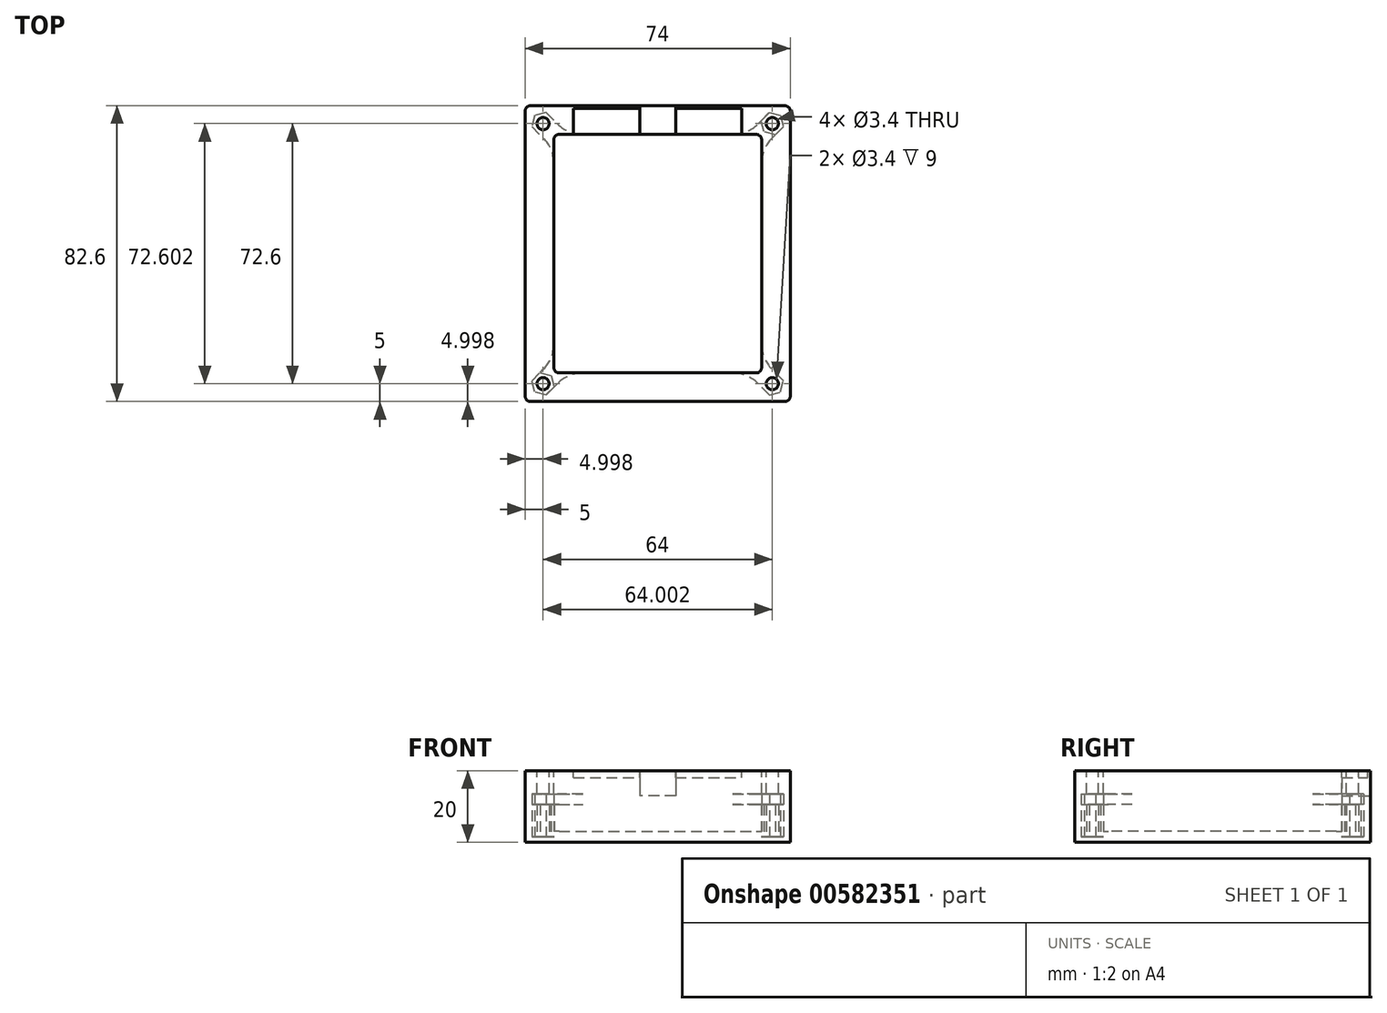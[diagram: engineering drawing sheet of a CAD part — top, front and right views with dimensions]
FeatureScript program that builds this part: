
annotation { "Feature Type Name" : "Feature", "Feature Type Description" : "" }
export const myFeature = defineFeature(function(context is Context, id is Id, definition is map)
    precondition{}
    {
        {
            var Q0;
            Q0=qCreatedBy(makeId("Top.planeOp"),FACE);
            var sketch = newSketch(context, id + "F0", { "sketchPlane" : qUnion([Q0])});
            skLineSegment(sketch, "E0.top", {"start": v(-37, -41.3) * mm, "end": v(37, -41.3) * mm});
            skLineSegment(sketch, "E0.left", {"start": v(-37, 31.3) * mm, "end": v(-37, -41.3) * mm});
            skLineSegment(sketch, "E0.right", {"start": v(37, 31.3) * mm, "end": v(37, -41.3) * mm});
            skLineSegment(sketch, "E1.top", {"start": v(-37, 41.3) * mm, "end": v(37, 41.3) * mm});
            skLineSegment(sketch, "E1.left", {"start": v(-37, 31.3) * mm, "end": v(-37, 41.3) * mm});
            skLineSegment(sketch, "E1.right", {"start": v(37, 31.3) * mm, "end": v(37, 41.3) * mm});
            skCircle(sketch, "E2", {"center": v(-32, 36.3) * mm, "radius": 1.7 * mm});
            skCircle(sketch, "E3.MirrorC", {"center": v(32, 36.3) * mm, "radius": 1.7 * mm});
            skCircle(sketch, "E4.MirrorC", {"center": v(32, -36.3) * mm, "radius": 1.7 * mm});
            skCircle(sketch, "E5.MirrorC", {"center": v(-32, -36.3) * mm, "radius": 1.7 * mm});
            skLineSegment(sketch, "E6", {"start": v(-37, 0) * mm, "end": v(37, 0) * mm, "construction": true});
            skLineSegment(sketch, "E7", {"start": v(0, 41.3) * mm, "end": v(0, -41.3) * mm, "construction": true});
            skLineSegment(sketch, "E8.0", {"start": v(-29, 33.3) * mm, "end": v(29, 33.3) * mm});
            skLineSegment(sketch, "E8.1", {"start": v(-29, 33.3) * mm, "end": v(-29, -33.3) * mm});
            skLineSegment(sketch, "E8.2", {"start": v(-29, -33.3) * mm, "end": v(29, -33.3) * mm});
            skLineSegment(sketch, "E8.3", {"start": v(29, 33.3) * mm, "end": v(29, -33.3) * mm});
            skCircle(sketch, "E9.cCircle", {"center": v(-32, -36.3) * mm, "radius": 2.8 * mm, "construction": true});
            skLineSegment(sketch, "E9.0", {"start": v(-35.13, -35.47) * mm, "end": v(-32.84, -33.18) * mm});
            skLineSegment(sketch, "E9.1", {"start": v(-32.84, -33.18) * mm, "end": v(-29.72, -34.02) * mm});
            skLineSegment(sketch, "E9.2", {"start": v(-29.72, -34.02) * mm, "end": v(-28.88, -37.14) * mm});
            skLineSegment(sketch, "E9.3", {"start": v(-28.88, -37.14) * mm, "end": v(-31.17, -39.43) * mm});
            skLineSegment(sketch, "E9.4", {"start": v(-31.17, -39.43) * mm, "end": v(-34.29, -38.59) * mm});
            skLineSegment(sketch, "E9.5", {"start": v(-34.29, -38.59) * mm, "end": v(-35.13, -35.47) * mm});
            skPoint(sketch, "E9.0.midPoint", {"position": v(-33.98, -34.32) * mm});
            skLineSegment(sketch, "E10", {"start": v(-37, -41.3) * mm, "end": v(-29, -33.3) * mm, "construction": true});
            skLineSegment(sketch, "E11", {"start": v(-32.84, -33.18) * mm, "end": v(-29, -29.34) * mm});
            skLineSegment(sketch, "E12", {"start": v(-28.88, -37.14) * mm, "end": v(-25.04, -33.3) * mm});
            skLineSegment(sketch, "E13.MirrorCS", {"start": v(29.72, -34.02) * mm, "end": v(28.88, -37.14) * mm});
            skLineSegment(sketch, "E14.MirrorCS", {"start": v(32.84, -33.18) * mm, "end": v(29.72, -34.02) * mm});
            skLineSegment(sketch, "E15.MirrorCS", {"start": v(28.88, -37.14) * mm, "end": v(25.04, -33.3) * mm});
            skLineSegment(sketch, "E16.MirrorCS", {"start": v(28.88, -37.14) * mm, "end": v(31.17, -39.43) * mm});
            skLineSegment(sketch, "E17.MirrorCS", {"start": v(31.17, -39.43) * mm, "end": v(34.29, -38.59) * mm});
            skLineSegment(sketch, "E18.MirrorCS", {"start": v(34.29, -38.59) * mm, "end": v(35.13, -35.47) * mm});
            skLineSegment(sketch, "E19.MirrorCS", {"start": v(32.84, -33.18) * mm, "end": v(29, -29.34) * mm});
            skLineSegment(sketch, "E20.MirrorCS", {"start": v(35.13, -35.47) * mm, "end": v(32.84, -33.18) * mm});
            skLineSegment(sketch, "E21.MirrorCS", {"start": v(35.13, 35.47) * mm, "end": v(32.84, 33.18) * mm});
            skLineSegment(sketch, "E22.MirrorCS", {"start": v(34.29, 38.59) * mm, "end": v(35.13, 35.47) * mm});
            skLineSegment(sketch, "E23.MirrorCS", {"start": v(31.17, 39.43) * mm, "end": v(34.29, 38.59) * mm});
            skLineSegment(sketch, "E24.MirrorCS", {"start": v(28.88, 37.14) * mm, "end": v(31.17, 39.43) * mm});
            skLineSegment(sketch, "E25.MirrorCS", {"start": v(28.88, 37.14) * mm, "end": v(25.04, 33.3) * mm});
            skLineSegment(sketch, "E26.MirrorCS", {"start": v(29.72, 34.02) * mm, "end": v(28.88, 37.14) * mm});
            skLineSegment(sketch, "E27.MirrorCS", {"start": v(32.84, 33.18) * mm, "end": v(29.72, 34.02) * mm});
            skLineSegment(sketch, "E28.MirrorCS", {"start": v(32.84, 33.18) * mm, "end": v(29, 29.34) * mm});
            skLineSegment(sketch, "E29.MirrorCS", {"start": v(-35.13, 35.47) * mm, "end": v(-32.84, 33.18) * mm});
            skPoint(sketch, "E30.MirrorP", {"position": v(-33.98, 34.32) * mm});
            skLineSegment(sketch, "E31.MirrorCS", {"start": v(-32.84, 33.18) * mm, "end": v(-29.72, 34.02) * mm});
            skLineSegment(sketch, "E32.MirrorCS", {"start": v(-34.29, 38.59) * mm, "end": v(-35.13, 35.47) * mm});
            skLineSegment(sketch, "E33.MirrorCS", {"start": v(-31.17, 39.43) * mm, "end": v(-34.29, 38.59) * mm});
            skLineSegment(sketch, "E34.MirrorCS", {"start": v(-28.88, 37.14) * mm, "end": v(-31.17, 39.43) * mm});
            skLineSegment(sketch, "E35.MirrorCS", {"start": v(-29.72, 34.02) * mm, "end": v(-28.88, 37.14) * mm});
            skLineSegment(sketch, "E36.MirrorCS", {"start": v(-32.84, 33.18) * mm, "end": v(-29, 29.34) * mm});
            skLineSegment(sketch, "E37.MirrorCS", {"start": v(-28.88, 37.14) * mm, "end": v(-25.04, 33.3) * mm});
            skSolve(sketch);
        }
        {
            var Q0;
            Q0=makeQuery(id+"F0.imprint","IMPRINT",FACE,{"disambiguationData":[TD([[makeQuery(id+"F0.imprint","IMPRINT",EDGE,{"derivedFrom":sQuery(id+"F0.wireOp",EDGE,"E0.top")}),1.0]])]});
            extrude(context, id + "F1", {"entities" : qUnion([Q0]), "depth" : 20 * mm, "offsetDistance" : 25 * mm});
        }
        {
            var Q0;
            {var subQ1=sQuery(id+"F0.wireOp",EDGE,"E8.0");var subQ8=sQuery(id+"F0.wireOp",EDGE,"E8.1");var subQ12=makeQuery(id+"F0.imprint","INTERSECT",VERTEX,{"derivedFrom":[subQ1,subQ8]});Q0=makeQuery(id+"F0.imprint","IMPRINT",FACE,{"disambiguationData":[TD([[makeQuery(id+"F0.imprint","IMPRINT",EDGE,{"disambiguationData":[TD([[subQ12,-1.0]])],"derivedFrom":subQ1}),-1.0]])]});}
            extrude(context, id + "F2", {"entities" : qUnion([Q0]), "operationType" : NewBodyOperationType.ADD, "depth" : 3 * mm, "offsetDistance" : 25 * mm});
        }
        {
            var Q0;
            Q0=makeQuery(id+"F0.imprint","IMPRINT",FACE,{"disambiguationData":[TD([[makeQuery(id+"F0.imprint","IMPRINT",EDGE,{"derivedFrom":sQuery(id+"F0.wireOp",EDGE,"E31.MirrorCS")}),-1.0]])]});
            var Q1;
            Q1=makeQuery(id+"F0.imprint","IMPRINT",FACE,{"disambiguationData":[TD([[makeQuery(id+"F0.imprint","IMPRINT",EDGE,{"derivedFrom":sQuery(id+"F0.wireOp",EDGE,"E2")}),-1.0]])]});
            var Q2;
            {var subQ4=sQuery(id+"F0.wireOp",EDGE,"E25.MirrorCS");Q2=makeQuery(id+"F0.imprint","IMPRINT",FACE,{"disambiguationData":[TD([[makeQuery(id+"F0.imprint","IMPRINT",EDGE,{"derivedFrom":subQ4}),1.0]])]});}
            var Q3;
            Q3=makeQuery(id+"F0.imprint","IMPRINT",FACE,{"disambiguationData":[TD([[makeQuery(id+"F0.imprint","IMPRINT",EDGE,{"derivedFrom":sQuery(id+"F0.wireOp",EDGE,"E3.MirrorC")}),1.0]])]});
            var Q4;
            Q4=makeQuery(id+"F0.imprint","IMPRINT",FACE,{"disambiguationData":[TD([[makeQuery(id+"F0.imprint","IMPRINT",EDGE,{"derivedFrom":sQuery(id+"F0.wireOp",EDGE,"E13.MirrorCS")}),-1.0]])]});
            var Q5;
            Q5=makeQuery(id+"F0.imprint","IMPRINT",FACE,{"disambiguationData":[TD([[makeQuery(id+"F0.imprint","IMPRINT",EDGE,{"derivedFrom":sQuery(id+"F0.wireOp",EDGE,"E9.1")}),1.0]])]});
            var Q6;
            Q6=makeQuery(id+"F0.imprint","IMPRINT",FACE,{"disambiguationData":[TD([[makeQuery(id+"F0.imprint","IMPRINT",EDGE,{"derivedFrom":sQuery(id+"F0.wireOp",EDGE,"E5.MirrorC")}),1.0]])]});
            var Q7;
            Q7=makeQuery(id+"F0.imprint","IMPRINT",FACE,{"disambiguationData":[TD([[makeQuery(id+"F0.imprint","IMPRINT",EDGE,{"derivedFrom":sQuery(id+"F0.wireOp",EDGE,"E4.MirrorC")}),-1.0]])]});
            extrude(context, id + "F3", {"entities" : qUnion([Q0, Q1, Q2, Q3, Q4, Q5, Q6, Q7]), "operationType" : NewBodyOperationType.ADD, "depth" : (8.5 + 2) * mm, "offsetDistance" : 25 * mm});
        }
        {
            var Q0;
            Q0=makeQuery(id+"F1.opExtrude","CAP_FACE",FACE,{"disambiguationData":[OSD([sQuery(id+"F0.wireOp",EDGE,"E0.top"),sQuery(id+"F0.wireOp",EDGE,"E0.left"),sQuery(id+"F0.wireOp",EDGE,"E0.right"),sQuery(id+"F0.wireOp",EDGE,"E1.top"),sQuery(id+"F0.wireOp",EDGE,"E1.left"),sQuery(id+"F0.wireOp",EDGE,"E1.right"),sQuery(id+"F0.wireOp",EDGE,"E8.0"),sQuery(id+"F0.wireOp",EDGE,"E8.1"),sQuery(id+"F0.wireOp",EDGE,"E8.2"),sQuery(id+"F0.wireOp",EDGE,"E8.3"),sQuery(id+"F0.wireOp",EDGE,"E9.0"),sQuery(id+"F0.wireOp",EDGE,"E9.3"),sQuery(id+"F0.wireOp",EDGE,"E9.4"),sQuery(id+"F0.wireOp",EDGE,"E9.5"),sQuery(id+"F0.wireOp",EDGE,"E11"),sQuery(id+"F0.wireOp",EDGE,"E12"),sQuery(id+"F0.wireOp",EDGE,"E16.MirrorCS"),sQuery(id+"F0.wireOp",EDGE,"E17.MirrorCS"),sQuery(id+"F0.wireOp",EDGE,"E18.MirrorCS"),sQuery(id+"F0.wireOp",EDGE,"E20.MirrorCS"),sQuery(id+"F0.wireOp",EDGE,"E19.MirrorCS"),sQuery(id+"F0.wireOp",EDGE,"E15.MirrorCS"),sQuery(id+"F0.wireOp",EDGE,"E21.MirrorCS"),sQuery(id+"F0.wireOp",EDGE,"E22.MirrorCS"),sQuery(id+"F0.wireOp",EDGE,"E23.MirrorCS"),sQuery(id+"F0.wireOp",EDGE,"E24.MirrorCS"),sQuery(id+"F0.wireOp",EDGE,"E25.MirrorCS"),sQuery(id+"F0.wireOp",EDGE,"E28.MirrorCS"),sQuery(id+"F0.wireOp",EDGE,"E29.MirrorCS"),sQuery(id+"F0.wireOp",EDGE,"E32.MirrorCS"),sQuery(id+"F0.wireOp",EDGE,"E33.MirrorCS"),sQuery(id+"F0.wireOp",EDGE,"E34.MirrorCS"),sQuery(id+"F0.wireOp",EDGE,"E36.MirrorCS"),sQuery(id+"F0.wireOp",EDGE,"E37.MirrorCS")])],"isStart":false});
            var sketch = newSketch(context, id + "F4", { "sketchPlane" : qUnion([Q0])});
            skLineSegment(sketch, "E38.0", {"start": v(-32.84, -33.18) * mm, "end": v(-29, -29.34) * mm});
            skPoint(sketch, "E39.0", {"position": v(-33.98, -34.32) * mm});
            skLineSegment(sketch, "E40.0", {"start": v(-35.13, -35.47) * mm, "end": v(-32.84, -33.18) * mm});
            skLineSegment(sketch, "E41.0", {"start": v(-34.29, -38.59) * mm, "end": v(-35.13, -35.47) * mm});
            skLineSegment(sketch, "E42.0", {"start": v(-31.17, -39.43) * mm, "end": v(-34.29, -38.59) * mm});
            skLineSegment(sketch, "E43.0", {"start": v(-28.88, -37.14) * mm, "end": v(-25.04, -33.3) * mm});
            skLineSegment(sketch, "E44.0", {"start": v(-28.88, -37.14) * mm, "end": v(-31.17, -39.43) * mm});
            skLineSegment(sketch, "E45.0", {"start": v(-29, 33.3) * mm, "end": v(-29, -33.3) * mm});
            skLineSegment(sketch, "E46.0", {"start": v(-29, -33.3) * mm, "end": v(29, -33.3) * mm});
            skLineSegment(sketch, "E47.0", {"start": v(28.88, -37.14) * mm, "end": v(25.04, -33.3) * mm});
            skLineSegment(sketch, "E48.0", {"start": v(32.84, -33.18) * mm, "end": v(29, -29.34) * mm});
            skLineSegment(sketch, "E49.0", {"start": v(35.13, -35.47) * mm, "end": v(32.84, -33.18) * mm});
            skLineSegment(sketch, "E50.0", {"start": v(32.84, -33.18) * mm, "end": v(29.72, -34.02) * mm});
            skLineSegment(sketch, "E51.0", {"start": v(29.72, -34.02) * mm, "end": v(28.88, -37.14) * mm});
            skLineSegment(sketch, "E52.0", {"start": v(28.88, -37.14) * mm, "end": v(31.17, -39.43) * mm});
            skLineSegment(sketch, "E53.0", {"start": v(31.17, -39.43) * mm, "end": v(34.29, -38.59) * mm});
            skLineSegment(sketch, "E54.0", {"start": v(34.29, -38.59) * mm, "end": v(35.13, -35.47) * mm});
            skLineSegment(sketch, "E55.0", {"start": v(-32.84, -33.18) * mm, "end": v(-29.72, -34.02) * mm});
            skLineSegment(sketch, "E56.0", {"start": v(-29.72, -34.02) * mm, "end": v(-28.88, -37.14) * mm});
            skLineSegment(sketch, "E57.0", {"start": v(-32.84, 33.18) * mm, "end": v(-29, 29.34) * mm});
            skLineSegment(sketch, "E58.0", {"start": v(-35.13, 35.47) * mm, "end": v(-32.84, 33.18) * mm});
            skLineSegment(sketch, "E59.0", {"start": v(-34.29, 38.59) * mm, "end": v(-35.13, 35.47) * mm});
            skLineSegment(sketch, "E60.0", {"start": v(-31.17, 39.43) * mm, "end": v(-34.29, 38.59) * mm});
            skLineSegment(sketch, "E61.0", {"start": v(-28.88, 37.14) * mm, "end": v(-31.17, 39.43) * mm});
            skLineSegment(sketch, "E62.0", {"start": v(-28.88, 37.14) * mm, "end": v(-25.04, 33.3) * mm});
            skLineSegment(sketch, "E63.0", {"start": v(-29, 33.3) * mm, "end": v(29, 33.3) * mm});
            skLineSegment(sketch, "E64.0", {"start": v(29, 33.3) * mm, "end": v(29, -33.3) * mm});
            skLineSegment(sketch, "E65.0", {"start": v(28.88, 37.14) * mm, "end": v(25.04, 33.3) * mm});
            skLineSegment(sketch, "E66.0", {"start": v(28.88, 37.14) * mm, "end": v(31.17, 39.43) * mm});
            skLineSegment(sketch, "E67.0", {"start": v(31.17, 39.43) * mm, "end": v(34.29, 38.59) * mm});
            skLineSegment(sketch, "E68.0", {"start": v(34.29, 38.59) * mm, "end": v(35.13, 35.47) * mm});
            skLineSegment(sketch, "E69.0", {"start": v(35.13, 35.47) * mm, "end": v(32.84, 33.18) * mm});
            skLineSegment(sketch, "E70.0", {"start": v(32.84, 33.18) * mm, "end": v(29, 29.34) * mm});
            skCircle(sketch, "E71.0", {"center": v(-32, 36.3) * mm, "radius": 1.7 * mm});
            skCircle(sketch, "E72.0", {"center": v(32, 36.3) * mm, "radius": 1.7 * mm});
            skCircle(sketch, "E73.0", {"center": v(-32, -36.3) * mm, "radius": 1.7 * mm});
            skCircle(sketch, "E74.0", {"center": v(32, -36.3) * mm, "radius": 1.7 * mm});
            skLineSegment(sketch, "E75.0", {"start": v(-32.84, 33.18) * mm, "end": v(-29.72, 34.02) * mm});
            skPoint(sketch, "E76.0", {"position": v(-29.3, 35.58) * mm});
            skLineSegment(sketch, "E77.0", {"start": v(-29.72, 34.02) * mm, "end": v(-28.88, 37.14) * mm});
            skLineSegment(sketch, "E78.0", {"start": v(32.84, 33.18) * mm, "end": v(29.72, 34.02) * mm});
            skLineSegment(sketch, "E79.0", {"start": v(29.72, 34.02) * mm, "end": v(28.88, 37.14) * mm});
            skSolve(sketch);
        }
        {
            var Q0;
            {var subQ1=sQuery(id+"F4.wireOp",EDGE,"E38.0");Q0=makeQuery(id+"F4.imprint","IMPRINT",FACE,{"disambiguationData":[TD([[makeQuery(id+"F4.imprint","IMPRINT",EDGE,{"derivedFrom":subQ1}),-1.0]])]});}
            var Q1;
            Q1=makeQuery(id+"F4.imprint","IMPRINT",FACE,{"disambiguationData":[TD([[makeQuery(id+"F4.imprint","IMPRINT",EDGE,{"derivedFrom":sQuery(id+"F4.wireOp",EDGE,"E40.0")}),-1.0]])]});
            var Q2;
            {var subQ1=sQuery(id+"F4.wireOp",EDGE,"E47.0");Q2=makeQuery(id+"F4.imprint","IMPRINT",FACE,{"disambiguationData":[TD([[makeQuery(id+"F4.imprint","IMPRINT",EDGE,{"derivedFrom":subQ1}),1.0]])]});}
            var Q3;
            Q3=makeQuery(id+"F4.imprint","IMPRINT",FACE,{"disambiguationData":[TD([[makeQuery(id+"F4.imprint","IMPRINT",EDGE,{"derivedFrom":sQuery(id+"F4.wireOp",EDGE,"E49.0")}),1.0]])]});
            var Q4;
            {var subQ1=sQuery(id+"F4.wireOp",EDGE,"E65.0");Q4=makeQuery(id+"F4.imprint","IMPRINT",FACE,{"disambiguationData":[TD([[makeQuery(id+"F4.imprint","IMPRINT",EDGE,{"derivedFrom":subQ1}),1.0]])]});}
            var Q5;
            Q5=makeQuery(id+"F4.imprint","IMPRINT",FACE,{"disambiguationData":[TD([[makeQuery(id+"F4.imprint","IMPRINT",EDGE,{"derivedFrom":sQuery(id+"F4.wireOp",EDGE,"E66.0")}),1.0]])]});
            var Q6;
            {var subQ4=sQuery(id+"F4.wireOp",EDGE,"E57.0");Q6=makeQuery(id+"F4.imprint","IMPRINT",FACE,{"disambiguationData":[TD([[makeQuery(id+"F4.imprint","IMPRINT",EDGE,{"derivedFrom":subQ4}),1.0]])]});}
            var Q7;
            Q7=makeQuery(id+"F4.imprint","IMPRINT",FACE,{"disambiguationData":[TD([[makeQuery(id+"F4.imprint","IMPRINT",EDGE,{"derivedFrom":sQuery(id+"F4.wireOp",EDGE,"E58.0")}),1.0]])]});
            extrude(context, id + "F5", {"entities" : qUnion([Q0, Q1, Q2, Q3, Q4, Q5, Q6, Q7]), "operationType" : NewBodyOperationType.ADD, "oppositeDirection" : true, "depth" : (8.5 - 2) * mm, "offsetDistance" : 25 * mm});
        }
        {
            var Q0;
            {var subQ0=sQuery(id+"F0.wireOp",EDGE,"E8.3");var subQ1=sQuery(id+"F0.wireOp",EDGE,"E28.MirrorCS");Q0=makeQuery(id+"F2.boolean.opBoolean","SPLIT",EDGE,{"disambiguationData":[topologyDisambiguationEdgeConnected([makeQuery(id+"F1.opExtrude","SWEPT_FACE",FACE,{"disambiguationData":[OSD([subQ0])]})])],"derivedFrom":makeQuery(id+"F1.opExtrude","SWEPT_EDGE",EDGE,{"disambiguationData":[OSD([subQ0,subQ1])]})});}
            var Q1;
            {var subQ0=sQuery(id+"F0.wireOp",EDGE,"E8.0");var subQ1=sQuery(id+"F0.wireOp",EDGE,"E25.MirrorCS");Q1=makeQuery(id+"F2.boolean.opBoolean","SPLIT",EDGE,{"disambiguationData":[topologyDisambiguationEdgeConnected([makeQuery(id+"F1.opExtrude","SWEPT_FACE",FACE,{"disambiguationData":[OSD([subQ0])]})])],"derivedFrom":makeQuery(id+"F1.opExtrude","SWEPT_EDGE",EDGE,{"disambiguationData":[OSD([subQ0,subQ1])]})});}
            var Q2;
            {var subQ0=sQuery(id+"F0.wireOp",EDGE,"E8.3");var subQ1=sQuery(id+"F0.wireOp",EDGE,"E19.MirrorCS");Q2=makeQuery(id+"F2.boolean.opBoolean","SPLIT",EDGE,{"disambiguationData":[topologyDisambiguationEdgeConnected([makeQuery(id+"F1.opExtrude","SWEPT_FACE",FACE,{"disambiguationData":[OSD([subQ0])]})])],"derivedFrom":makeQuery(id+"F1.opExtrude","SWEPT_EDGE",EDGE,{"disambiguationData":[OSD([subQ0,subQ1])]})});}
            var Q3;
            {var subQ0=sQuery(id+"F0.wireOp",EDGE,"E8.2");var subQ1=sQuery(id+"F0.wireOp",EDGE,"E15.MirrorCS");Q3=makeQuery(id+"F2.boolean.opBoolean","SPLIT",EDGE,{"disambiguationData":[topologyDisambiguationEdgeConnected([makeQuery(id+"F1.opExtrude","SWEPT_FACE",FACE,{"disambiguationData":[OSD([subQ0])]})])],"derivedFrom":makeQuery(id+"F1.opExtrude","SWEPT_EDGE",EDGE,{"disambiguationData":[OSD([subQ0,subQ1])]})});}
            var Q4;
            {var subQ0=sQuery(id+"F0.wireOp",EDGE,"E8.1");var subQ1=sQuery(id+"F0.wireOp",EDGE,"E36.MirrorCS");Q4=makeQuery(id+"F2.boolean.opBoolean","SPLIT",EDGE,{"disambiguationData":[topologyDisambiguationEdgeConnected([makeQuery(id+"F1.opExtrude","SWEPT_FACE",FACE,{"disambiguationData":[OSD([subQ0])]})])],"derivedFrom":makeQuery(id+"F1.opExtrude","SWEPT_EDGE",EDGE,{"disambiguationData":[OSD([subQ0,subQ1])]})});}
            var Q5;
            {var subQ0=sQuery(id+"F0.wireOp",EDGE,"E8.0");var subQ1=sQuery(id+"F0.wireOp",EDGE,"E37.MirrorCS");Q5=makeQuery(id+"F2.boolean.opBoolean","SPLIT",EDGE,{"disambiguationData":[topologyDisambiguationEdgeConnected([makeQuery(id+"F1.opExtrude","SWEPT_FACE",FACE,{"disambiguationData":[OSD([subQ0])]})])],"derivedFrom":makeQuery(id+"F1.opExtrude","SWEPT_EDGE",EDGE,{"disambiguationData":[OSD([subQ0,subQ1])]})});}
            var Q6;
            {var subQ0=sQuery(id+"F0.wireOp",EDGE,"E8.2");var subQ1=sQuery(id+"F0.wireOp",EDGE,"E12");Q6=makeQuery(id+"F2.boolean.opBoolean","SPLIT",EDGE,{"disambiguationData":[topologyDisambiguationEdgeConnected([makeQuery(id+"F1.opExtrude","SWEPT_FACE",FACE,{"disambiguationData":[OSD([subQ0])]})])],"derivedFrom":makeQuery(id+"F1.opExtrude","SWEPT_EDGE",EDGE,{"disambiguationData":[OSD([subQ0,subQ1])]})});}
            var Q7;
            {var subQ0=sQuery(id+"F0.wireOp",EDGE,"E8.1");var subQ1=sQuery(id+"F0.wireOp",EDGE,"E11");Q7=makeQuery(id+"F2.boolean.opBoolean","SPLIT",EDGE,{"disambiguationData":[topologyDisambiguationEdgeConnected([makeQuery(id+"F1.opExtrude","SWEPT_FACE",FACE,{"disambiguationData":[OSD([subQ0])]})])],"derivedFrom":makeQuery(id+"F1.opExtrude","SWEPT_EDGE",EDGE,{"disambiguationData":[OSD([subQ0,subQ1])]})});}
            fillet(context, id + "F6", {"entities" : qUnion([Q0, Q1, Q2, Q3, Q4, Q5, Q6, Q7]), "radius" : 10 * mm, "tangentPropagation" : true, "allowEdgeOverflow" : false});
        }
        {
            var Q0;
            Q0=makeQuery(id+"F1.opExtrude","SWEPT_EDGE",EDGE,{"disambiguationData":[OSD([sQuery(id+"F0.wireOp",EDGE,"E0.top"),sQuery(id+"F0.wireOp",EDGE,"E0.left")])]});
            var Q1;
            Q1=makeQuery(id+"F1.opExtrude","SWEPT_EDGE",EDGE,{"disambiguationData":[OSD([sQuery(id+"F0.wireOp",EDGE,"E0.top"),sQuery(id+"F0.wireOp",EDGE,"E0.right")])]});
            var Q2;
            Q2=makeQuery(id+"F1.opExtrude","SWEPT_EDGE",EDGE,{"disambiguationData":[OSD([sQuery(id+"F0.wireOp",EDGE,"E1.top"),sQuery(id+"F0.wireOp",EDGE,"E1.left")])]});
            var Q3;
            Q3=makeQuery(id+"F1.opExtrude","SWEPT_EDGE",EDGE,{"disambiguationData":[OSD([sQuery(id+"F0.wireOp",EDGE,"E1.top"),sQuery(id+"F0.wireOp",EDGE,"E1.right")])]});
            var Q4;
            Q4=makeQuery(id+"F3.opExtrude","SWEPT_EDGE",EDGE,{"disambiguationData":[OSD([sQuery(id+"F0.wireOp",EDGE,"E8.0"),sQuery(id+"F0.wireOp",EDGE,"E8.1")])]});
            var Q5;
            Q5=makeQuery(id+"F5.opExtrude","SWEPT_EDGE",EDGE,{"disambiguationData":[OSD([sQuery(id+"F4.wireOp",EDGE,"E45.0"),sQuery(id+"F4.wireOp",EDGE,"E63.0")])]});
            var Q6;
            Q6=makeQuery(id+"F3.opExtrude","SWEPT_EDGE",EDGE,{"disambiguationData":[OSD([sQuery(id+"F0.wireOp",EDGE,"E8.0"),sQuery(id+"F0.wireOp",EDGE,"E8.3")])]});
            var Q7;
            Q7=makeQuery(id+"F5.opExtrude","SWEPT_EDGE",EDGE,{"disambiguationData":[OSD([sQuery(id+"F4.wireOp",EDGE,"E63.0"),sQuery(id+"F4.wireOp",EDGE,"E64.0")])]});
            var Q8;
            Q8=makeQuery(id+"F3.opExtrude","SWEPT_EDGE",EDGE,{"disambiguationData":[OSD([sQuery(id+"F0.wireOp",EDGE,"E8.1"),sQuery(id+"F0.wireOp",EDGE,"E8.2")])]});
            var Q9;
            Q9=makeQuery(id+"F5.opExtrude","SWEPT_EDGE",EDGE,{"disambiguationData":[OSD([sQuery(id+"F4.wireOp",EDGE,"E45.0"),sQuery(id+"F4.wireOp",EDGE,"E46.0")])]});
            var Q10;
            Q10=makeQuery(id+"F3.opExtrude","SWEPT_EDGE",EDGE,{"disambiguationData":[OSD([sQuery(id+"F0.wireOp",EDGE,"E8.2"),sQuery(id+"F0.wireOp",EDGE,"E8.3")])]});
            var Q11;
            Q11=makeQuery(id+"F5.opExtrude","SWEPT_EDGE",EDGE,{"disambiguationData":[OSD([sQuery(id+"F4.wireOp",EDGE,"E46.0"),sQuery(id+"F4.wireOp",EDGE,"E64.0")])]});
            fillet(context, id + "F7", {"entities" : qUnion([Q0, Q1, Q2, Q3, Q4, Q5, Q6, Q7, Q8, Q9, Q10, Q11]), "radius" : 1.5 * mm, "tangentPropagation" : true, "allowEdgeOverflow" : false});
        }
        {
            var Q0;
            Q0=makeQuery(id+"F0.imprint","IMPRINT",FACE,{"disambiguationData":[TD([[makeQuery(id+"F0.imprint","IMPRINT",EDGE,{"derivedFrom":sQuery(id+"F0.wireOp",EDGE,"E4.MirrorC")}),1.0]])]});
            var Q1;
            Q1=makeQuery(id+"F0.imprint","IMPRINT",FACE,{"disambiguationData":[TD([[makeQuery(id+"F0.imprint","IMPRINT",EDGE,{"derivedFrom":sQuery(id+"F0.wireOp",EDGE,"E3.MirrorC")}),-1.0]])]});
            var Q2;
            Q2=makeQuery(id+"F0.imprint","IMPRINT",FACE,{"disambiguationData":[TD([[makeQuery(id+"F0.imprint","IMPRINT",EDGE,{"derivedFrom":sQuery(id+"F0.wireOp",EDGE,"E5.MirrorC")}),-1.0]])]});
            var Q3;
            Q3=makeQuery(id+"F0.imprint","IMPRINT",FACE,{"disambiguationData":[TD([[makeQuery(id+"F0.imprint","IMPRINT",EDGE,{"derivedFrom":sQuery(id+"F0.wireOp",EDGE,"E2")}),1.0]])]});
            extrude(context, id + "F8", {"entities" : qUnion([Q0, Q1, Q2, Q3]), "operationType" : NewBodyOperationType.ADD, "depth" : 1.5 * mm, "offsetDistance" : 25 * mm});
        }
        {
            var Q0;
            Q0=makeQuery(id+"F1.opExtrude","SWEPT_FACE",FACE,{"disambiguationData":[OSD([sQuery(id+"F0.wireOp",EDGE,"E1.top")])]});
            var sketch = newSketch(context, id + "F9", { "sketchPlane" : qUnion([Q0])});
            skLineSegment(sketch, "E80.bottom", {"start": v(-5, 20) * mm, "end": v(5, 20) * mm});
            skLineSegment(sketch, "E80.top", {"start": v(-5, 13) * mm, "end": v(5, 13) * mm});
            skLineSegment(sketch, "E80.left", {"start": v(-5, 20) * mm, "end": v(-5, 13) * mm});
            skLineSegment(sketch, "E80.right", {"start": v(5, 20) * mm, "end": v(5, 13) * mm});
            skSolve(sketch);
        }
        {
            var Q0;
            Q0=makeQuery(id+"F9.imprint","IMPRINT",FACE,{"disambiguationData":[TD([[makeQuery(id+"F9.imprint","IMPRINT",EDGE,{"derivedFrom":sQuery(id+"F9.wireOp",EDGE,"E80.bottom")}),1.0]])]});
            extrude(context, id + "F10", {"entities" : qUnion([Q0]), "operationType" : NewBodyOperationType.REMOVE, "oppositeDirection" : true, "depth" : 10 * mm, "offsetDistance" : 25 * mm});
        }
        {
            var Q0;
            Q0=qCreatedBy(makeId("Top.planeOp"),FACE);
            var sketch = newSketch(context, id + "F11", { "sketchPlane" : qUnion([Q0])});
            skLineSegment(sketch, "E81.bottom", {"start": v(22.5, 40.2) * mm, "end": v(22.5, -11.8) * mm, "construction": true});
            skLineSegment(sketch, "E81.top", {"start": v(-22.5, 40.2) * mm, "end": v(-22.5, -11.8) * mm, "construction": true});
            skLineSegment(sketch, "E81.left", {"start": v(22.5, 40.2) * mm, "end": v(-22.5, 40.2) * mm, "construction": true});
            skLineSegment(sketch, "E81.right", {"start": v(22.5, -11.8) * mm, "end": v(-22.5, -11.8) * mm, "construction": true});
            skPoint(sketch, "E81.middle", {"position": v(0, 14.2) * mm});
            skCircle(sketch, "E82", {"center": v(-19, -8.3) * mm, "radius": 1.5 * mm, "construction": true});
            skCircle(sketch, "E83.cCircle", {"center": v(-19, -8.3) * mm, "radius": 2.75 * mm, "construction": true});
            skLineSegment(sketch, "E83.0", {"start": v(-20.59, -5.55) * mm, "end": v(-17.41, -5.55) * mm, "construction": true});
            skLineSegment(sketch, "E83.1", {"start": v(-17.41, -5.55) * mm, "end": v(-15.82, -8.3) * mm, "construction": true});
            skLineSegment(sketch, "E83.2", {"start": v(-15.82, -8.3) * mm, "end": v(-17.41, -11.05) * mm, "construction": true});
            skLineSegment(sketch, "E83.3", {"start": v(-17.41, -11.05) * mm, "end": v(-20.59, -11.05) * mm, "construction": true});
            skLineSegment(sketch, "E83.4", {"start": v(-20.59, -11.05) * mm, "end": v(-22.18, -8.3) * mm, "construction": true});
            skLineSegment(sketch, "E83.5", {"start": v(-22.18, -8.3) * mm, "end": v(-20.59, -5.55) * mm, "construction": true});
            skPoint(sketch, "E83.0.midPoint", {"position": v(-19, -5.55) * mm});
            skLineSegment(sketch, "E84.MirrorCS", {"start": v(-20.59, 33.95) * mm, "end": v(-17.41, 33.95) * mm, "construction": true});
            skCircle(sketch, "E85.MirrorC", {"center": v(-19, 36.7) * mm, "radius": 1.5 * mm, "construction": true});
            skCircle(sketch, "E86.MirrorC", {"center": v(-19, 36.7) * mm, "radius": 2.75 * mm, "construction": true});
            skLineSegment(sketch, "E87.MirrorCS", {"start": v(-17.41, 33.95) * mm, "end": v(-15.82, 36.7) * mm, "construction": true});
            skPoint(sketch, "E88.MirrorP", {"position": v(-19, 33.95) * mm});
            skLineSegment(sketch, "E89.MirrorCS", {"start": v(-22.18, 36.7) * mm, "end": v(-20.59, 33.95) * mm, "construction": true});
            skLineSegment(sketch, "E90.MirrorCS", {"start": v(-20.59, 39.45) * mm, "end": v(-22.18, 36.7) * mm, "construction": true});
            skLineSegment(sketch, "E91.MirrorCS", {"start": v(-15.82, 36.7) * mm, "end": v(-17.41, 39.45) * mm, "construction": true});
            skLineSegment(sketch, "E92.MirrorCS", {"start": v(-17.41, 39.45) * mm, "end": v(-20.59, 39.45) * mm, "construction": true});
            skLineSegment(sketch, "E93.MirrorCS", {"start": v(20.59, 33.95) * mm, "end": v(17.41, 33.95) * mm, "construction": true});
            skLineSegment(sketch, "E94.MirrorCS", {"start": v(22.18, -8.3) * mm, "end": v(20.59, -5.55) * mm, "construction": true});
            skLineSegment(sketch, "E95.MirrorCS", {"start": v(20.59, -11.05) * mm, "end": v(22.18, -8.3) * mm, "construction": true});
            skLineSegment(sketch, "E96.MirrorCS", {"start": v(15.82, -8.3) * mm, "end": v(17.41, -11.05) * mm, "construction": true});
            skLineSegment(sketch, "E97.MirrorCS", {"start": v(17.41, -5.55) * mm, "end": v(15.82, -8.3) * mm, "construction": true});
            skLineSegment(sketch, "E98.MirrorCS", {"start": v(20.59, -5.55) * mm, "end": v(17.41, -5.55) * mm, "construction": true});
            skLineSegment(sketch, "E99.MirrorCS", {"start": v(20.59, 39.45) * mm, "end": v(22.18, 36.7) * mm, "construction": true});
            skLineSegment(sketch, "E100.MirrorCS", {"start": v(17.41, 39.45) * mm, "end": v(20.59, 39.45) * mm, "construction": true});
            skLineSegment(sketch, "E101.MirrorCS", {"start": v(22.18, 36.7) * mm, "end": v(20.59, 33.95) * mm, "construction": true});
            skLineSegment(sketch, "E102.MirrorCS", {"start": v(15.82, 36.7) * mm, "end": v(17.41, 39.45) * mm, "construction": true});
            skLineSegment(sketch, "E103.MirrorCS", {"start": v(17.41, 33.95) * mm, "end": v(15.82, 36.7) * mm, "construction": true});
            skLineSegment(sketch, "E104.MirrorCS", {"start": v(17.41, -11.05) * mm, "end": v(20.59, -11.05) * mm, "construction": true});
            skCircle(sketch, "E105.MirrorC", {"center": v(19, -8.3) * mm, "radius": 2.75 * mm, "construction": true});
            skPoint(sketch, "E106.MirrorP", {"position": v(19, 33.95) * mm});
            skCircle(sketch, "E107.MirrorC", {"center": v(19, -8.3) * mm, "radius": 1.5 * mm, "construction": true});
            skCircle(sketch, "E108.MirrorC", {"center": v(19, 36.7) * mm, "radius": 2.75 * mm, "construction": true});
            skCircle(sketch, "E109.MirrorC", {"center": v(19, 36.7) * mm, "radius": 1.5 * mm, "construction": true});
            skPoint(sketch, "E110.MirrorP", {"position": v(19, -5.55) * mm});
            skLineSegment(sketch, "E111", {"start": v(-35.53, 40.2) * mm, "end": v(30.9, 40.2) * mm, "construction": true});
            skSolve(sketch);
        }
        {
            var Q0;
            {var subQ0=sQuery(id+"F4.wireOp",EDGE,"E64.0");var subQ1=sQuery(id+"F4.wireOp",EDGE,"E63.0");var subQ2=sQuery(id+"F4.wireOp",EDGE,"E46.0");var subQ3=sQuery(id+"F4.wireOp",EDGE,"E45.0");Q0=makeQuery(id+"F5.boolean.opBoolean","MERGE",FACE,{"derivedFrom":[makeQuery(id+"F1.opExtrude","CAP_FACE",FACE,{"disambiguationData":[OSD([sQuery(id+"F0.wireOp",EDGE,"E0.top"),sQuery(id+"F0.wireOp",EDGE,"E0.left"),sQuery(id+"F0.wireOp",EDGE,"E0.right"),sQuery(id+"F0.wireOp",EDGE,"E1.top"),sQuery(id+"F0.wireOp",EDGE,"E1.left"),sQuery(id+"F0.wireOp",EDGE,"E1.right"),sQuery(id+"F0.wireOp",EDGE,"E8.0"),sQuery(id+"F0.wireOp",EDGE,"E8.1"),sQuery(id+"F0.wireOp",EDGE,"E8.2"),sQuery(id+"F0.wireOp",EDGE,"E8.3"),sQuery(id+"F0.wireOp",EDGE,"E9.0"),sQuery(id+"F0.wireOp",EDGE,"E9.3"),sQuery(id+"F0.wireOp",EDGE,"E9.4"),sQuery(id+"F0.wireOp",EDGE,"E9.5"),sQuery(id+"F0.wireOp",EDGE,"E11"),sQuery(id+"F0.wireOp",EDGE,"E12"),sQuery(id+"F0.wireOp",EDGE,"E16.MirrorCS"),sQuery(id+"F0.wireOp",EDGE,"E17.MirrorCS"),sQuery(id+"F0.wireOp",EDGE,"E18.MirrorCS"),sQuery(id+"F0.wireOp",EDGE,"E20.MirrorCS"),sQuery(id+"F0.wireOp",EDGE,"E19.MirrorCS"),sQuery(id+"F0.wireOp",EDGE,"E15.MirrorCS"),sQuery(id+"F0.wireOp",EDGE,"E21.MirrorCS"),sQuery(id+"F0.wireOp",EDGE,"E22.MirrorCS"),sQuery(id+"F0.wireOp",EDGE,"E23.MirrorCS"),sQuery(id+"F0.wireOp",EDGE,"E24.MirrorCS"),sQuery(id+"F0.wireOp",EDGE,"E25.MirrorCS"),sQuery(id+"F0.wireOp",EDGE,"E28.MirrorCS"),sQuery(id+"F0.wireOp",EDGE,"E29.MirrorCS"),sQuery(id+"F0.wireOp",EDGE,"E32.MirrorCS"),sQuery(id+"F0.wireOp",EDGE,"E33.MirrorCS"),sQuery(id+"F0.wireOp",EDGE,"E34.MirrorCS"),sQuery(id+"F0.wireOp",EDGE,"E36.MirrorCS"),sQuery(id+"F0.wireOp",EDGE,"E37.MirrorCS")])],"isStart":false}),makeQuery(id+"F5.opExtrude","CAP_FACE",FACE,{"disambiguationData":[OSD([sQuery(id+"F4.wireOp",EDGE,"E38.0"),sQuery(id+"F4.wireOp",EDGE,"E40.0"),sQuery(id+"F4.wireOp",EDGE,"E41.0"),sQuery(id+"F4.wireOp",EDGE,"E42.0"),sQuery(id+"F4.wireOp",EDGE,"E43.0"),sQuery(id+"F4.wireOp",EDGE,"E44.0"),subQ3,subQ2,sQuery(id+"F4.wireOp",EDGE,"E73.0")])],"isStart":true}),makeQuery(id+"F5.opExtrude","CAP_FACE",FACE,{"disambiguationData":[OSD([subQ3,sQuery(id+"F4.wireOp",EDGE,"E57.0"),sQuery(id+"F4.wireOp",EDGE,"E58.0"),sQuery(id+"F4.wireOp",EDGE,"E59.0"),sQuery(id+"F4.wireOp",EDGE,"E60.0"),sQuery(id+"F4.wireOp",EDGE,"E61.0"),sQuery(id+"F4.wireOp",EDGE,"E62.0"),subQ1,sQuery(id+"F4.wireOp",EDGE,"E71.0")])],"isStart":true}),makeQuery(id+"F5.opExtrude","CAP_FACE",FACE,{"disambiguationData":[OSD([subQ2,sQuery(id+"F4.wireOp",EDGE,"E47.0"),sQuery(id+"F4.wireOp",EDGE,"E48.0"),sQuery(id+"F4.wireOp",EDGE,"E49.0"),sQuery(id+"F4.wireOp",EDGE,"E52.0"),sQuery(id+"F4.wireOp",EDGE,"E53.0"),sQuery(id+"F4.wireOp",EDGE,"E54.0"),subQ0,sQuery(id+"F4.wireOp",EDGE,"E74.0")])],"isStart":true}),makeQuery(id+"F5.opExtrude","CAP_FACE",FACE,{"disambiguationData":[OSD([subQ1,subQ0,sQuery(id+"F4.wireOp",EDGE,"E65.0"),sQuery(id+"F4.wireOp",EDGE,"E66.0"),sQuery(id+"F4.wireOp",EDGE,"E67.0"),sQuery(id+"F4.wireOp",EDGE,"E68.0"),sQuery(id+"F4.wireOp",EDGE,"E69.0"),sQuery(id+"F4.wireOp",EDGE,"E70.0"),sQuery(id+"F4.wireOp",EDGE,"E72.0")])],"isStart":true})]});}
            var sketch = newSketch(context, id + "F12", { "sketchPlane" : qUnion([Q0])});
            skLineSegment(sketch, "E112", {"start": v(-23.5, 33.3) * mm, "end": v(-23.5, 40.5) * mm});
            skLineSegment(sketch, "E113", {"start": v(-23.5, 40.5) * mm, "end": v(23.5, 40.5) * mm});
            skLineSegment(sketch, "E114", {"start": v(23.5, 40.5) * mm, "end": v(23.5, 33.3) * mm});
            skLineSegment(sketch, "E115", {"start": v(-23.5, 33.3) * mm, "end": v(23.5, 33.3) * mm});
            skSolve(sketch);
        }
        {
            var Q0;
            {var subQ0=sQuery(id+"F12.wireOp",EDGE,"E112");Q0=makeQuery(id+"F12.imprint","IMPRINT",FACE,{"disambiguationData":[TD([[makeQuery(id+"F12.imprint","IMPRINT",EDGE,{"derivedFrom":subQ0}),-1.0]])]});}
            var Q1;
            {var subQ0=sQuery(id+"F12.wireOp",EDGE,"E114");Q1=makeQuery(id+"F12.imprint","IMPRINT",FACE,{"disambiguationData":[TD([[makeQuery(id+"F12.imprint","IMPRINT",EDGE,{"derivedFrom":subQ0}),-1.0]])]});}
            extrude(context, id + "F13", {"entities" : qUnion([Q0, Q1]), "operationType" : NewBodyOperationType.REMOVE, "oppositeDirection" : true, "depth" : 2 * mm, "offsetDistance" : 25 * mm});
        }
    });
